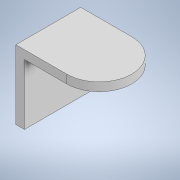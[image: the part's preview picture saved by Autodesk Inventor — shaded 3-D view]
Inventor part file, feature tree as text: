
AUTODESK INVENTOR PART (.ipt)
format: ipt  version: 2020 (Build 240168000, 168)  size: 136,704 bytes
history: native  units: in
note: dims shown in document units (in); Inventor stores cm internally (conversion verified against a paired STEP export)
features: sketch x4, extrude x3
ambient origin geometry x8: Origin, YZ Plane, XZ Plane, XY Plane, X Axis, Y Axis, Z Axis, Center Point
bodies: Solid1 (feature_tree)
feature tree (7):
  extrude  "Extrusion1"  Depth=0.0787in TaperAngle=0.0deg
  extrude  "Extrusion2"  Depth=0.1969in
  sketch  "Sketch3"  dims[d12=1.6in d13=0.0in]
  extrude  "Extrusion3"  [1 undecoded]
  sketch  "Sketch1"  dims[d1=1.5748in d2=1.5in d3=1.0in d4=0.315in d5=0.0591in d6=360.0deg d7=0.0787in d8=0.0in]
  sketch  "Sketch2"  dims[d9=0.1181in d10=0.0in d11=0.1969in]
  sketch  "Sketch4"
note: 1 required parameter value undecoded (feature->parameter linkage not recoverable at this tier; creation-order binding heuristic only, values carry confidence <= 0.55)
